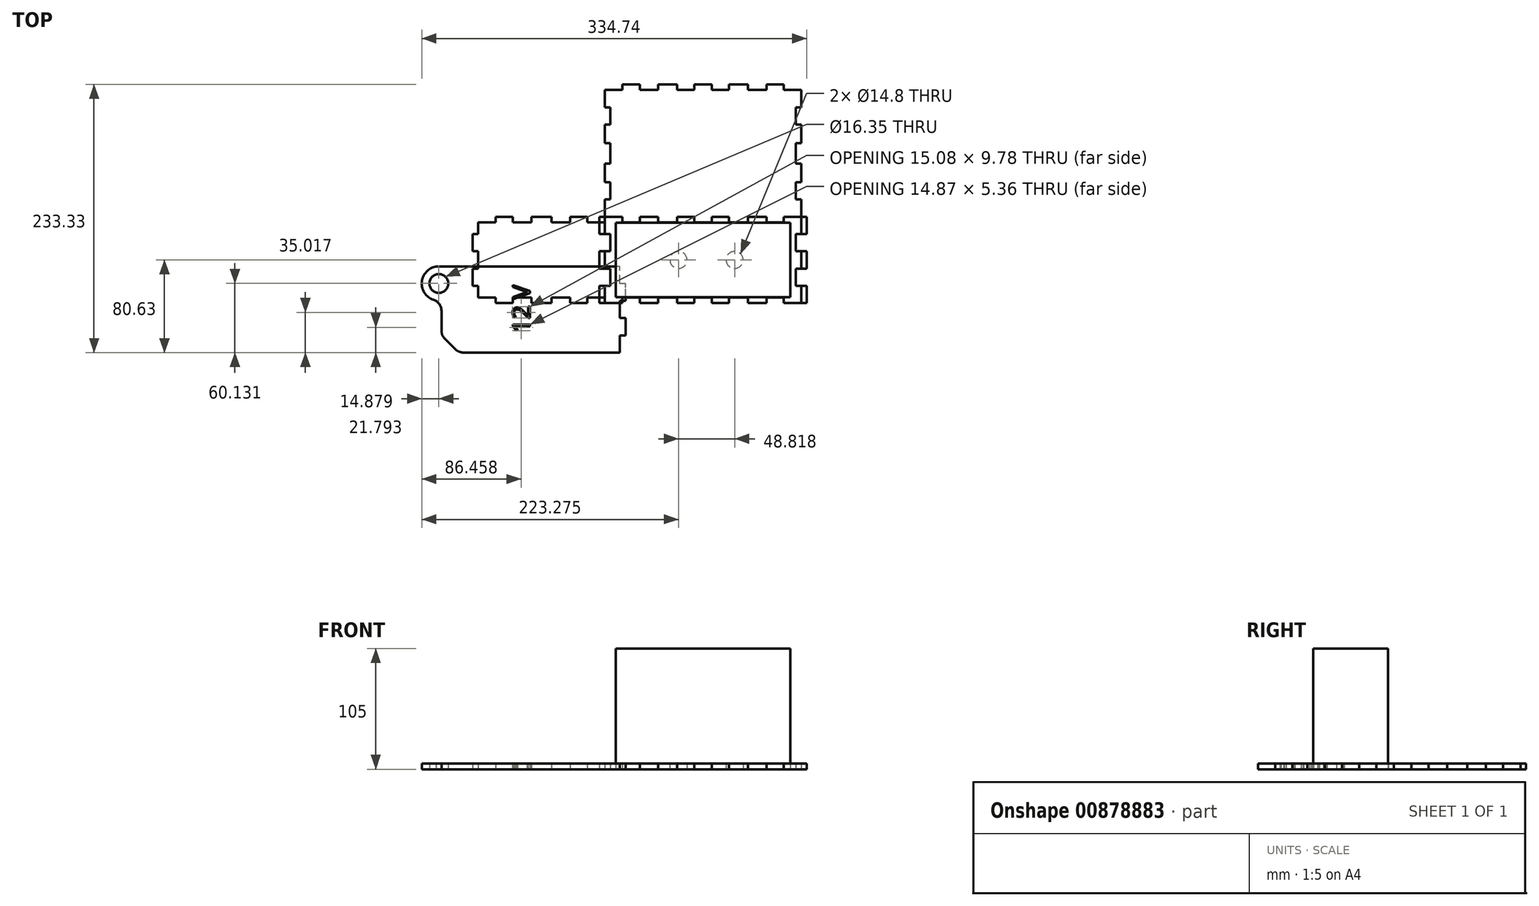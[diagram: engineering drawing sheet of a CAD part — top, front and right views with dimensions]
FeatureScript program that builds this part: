
annotation { "Feature Type Name" : "Feature", "Feature Type Description" : "" }
export const myFeature = defineFeature(function(context is Context, id is Id, definition is map)
    precondition{}
    {
        {
            assignVariable(context, id + "F0", {"name" : "MDF", "anyValue" : 4.8});
        }
        {
            var Q0;
            Q0=qCreatedBy(makeId("Top.planeOp"),FACE);
            var sketch = newSketch(context, id + "F1", { "sketchPlane" : qUnion([Q0])});
            skLineSegment(sketch, "E0", {"start": v(0, 32.5) * mm, "end": v(-76, 32.5) * mm});
            skLineSegment(sketch, "E1", {"start": v(-76, 32.5) * mm, "end": v(-76, 0) * mm});
            skLineSegment(sketch, "E2.MirrorCS", {"start": v(0, 32.5) * mm, "end": v(76, 32.5) * mm});
            skLineSegment(sketch, "E3.MirrorCS", {"start": v(76, 32.5) * mm, "end": v(76, 0) * mm});
            skLineSegment(sketch, "E4.MirrorCS", {"start": v(-76, -32.5) * mm, "end": v(-76, 0) * mm});
            skLineSegment(sketch, "E5.MirrorCS", {"start": v(0, -32.5) * mm, "end": v(-76, -32.5) * mm});
            skLineSegment(sketch, "E6.MirrorCS", {"start": v(0, -32.5) * mm, "end": v(76, -32.5) * mm});
            skLineSegment(sketch, "E7.MirrorCS", {"start": v(76, -32.5) * mm, "end": v(76, 0) * mm});
            skSolve(sketch);
        }
        {
            var Q0;
            Q0=makeQuery(id+"F1.imprint","IMPRINT",FACE,{"disambiguationData":[TD([[makeQuery(id+"F1.imprint","IMPRINT",EDGE,{"derivedFrom":sQuery(id+"F1.wireOp",EDGE,"E0")}),1.0]])]});
            extrude(context, id + "F2", {"entities" : qUnion([Q0]), "depth" : 105 * mm, "offsetDistance" : 25 * mm});
        }
        {
            var Q0;
            Q0=qCreatedBy(makeId("Top.planeOp"),FACE);
            var sketch = newSketch(context, id + "F3", { "sketchPlane" : qUnion([Q0])});
            skLineSegment(sketch, "E8", {"start": v(-85.3, 37.5) * mm, "end": v(-70.1, 37.5) * mm});
            skLineSegment(sketch, "E9", {"start": v(85.3, 37.5) * mm, "end": v(85.3, 22.5) * mm});
            skLineSegment(sketch, "E10", {"start": v(-85.3, -37.5) * mm, "end": v(-85.3, -22.5) * mm});
            skLineSegment(sketch, "E11", {"start": v(-55.1, 37.5) * mm, "end": v(-38.95, 37.5) * mm});
            skLineSegment(sketch, "E12", {"start": v(-70.1, 37.5) * mm, "end": v(-70.1, 32.7) * mm});
            skLineSegment(sketch, "E13", {"start": v(-70.1, 32.7) * mm, "end": v(-55.1, 32.7) * mm});
            skLineSegment(sketch, "E14", {"start": v(-55.1, 32.7) * mm, "end": v(-55.1, 37.5) * mm});
            skLineSegment(sketch, "E15.1.0.0", {"start": v(-38.95, 37.5) * mm, "end": v(-38.95, 32.7) * mm});
            skLineSegment(sketch, "E15.1.0.2", {"start": v(-22.5, 32.7) * mm, "end": v(-22.5, 37.5) * mm});
            skLineSegment(sketch, "E15.2.0.0", {"start": v(-7.5, 37.5) * mm, "end": v(-7.5, 32.7) * mm});
            skLineSegment(sketch, "E16.trimOffspring", {"start": v(-22.5, 37.5) * mm, "end": v(-7.5, 37.5) * mm});
            skLineSegment(sketch, "E17", {"start": v(-38.95, 32.7) * mm, "end": v(-22.5, 32.7) * mm});
            skLineSegment(sketch, "E18.MirrorCS", {"start": v(70.1, 37.5) * mm, "end": v(70.1, 32.7) * mm});
            skLineSegment(sketch, "E19.MirrorCS", {"start": v(55.1, 32.7) * mm, "end": v(55.1, 37.5) * mm});
            skLineSegment(sketch, "E20.MirrorCS", {"start": v(55.1, 37.5) * mm, "end": v(38.95, 37.5) * mm});
            skLineSegment(sketch, "E21.MirrorCS", {"start": v(38.95, 37.5) * mm, "end": v(38.95, 32.7) * mm});
            skLineSegment(sketch, "E22.MirrorCS", {"start": v(22.5, 32.7) * mm, "end": v(22.5, 37.5) * mm});
            skLineSegment(sketch, "E23.MirrorCS", {"start": v(22.5, 37.5) * mm, "end": v(7.5, 37.5) * mm});
            skLineSegment(sketch, "E24.MirrorCS", {"start": v(7.5, 37.5) * mm, "end": v(7.5, 32.7) * mm});
            skLineSegment(sketch, "E25", {"start": v(-7.5, 32.7) * mm, "end": v(7.5, 32.7) * mm});
            skLineSegment(sketch, "E26", {"start": v(22.5, 32.7) * mm, "end": v(38.95, 32.7) * mm});
            skLineSegment(sketch, "E27", {"start": v(55.1, 32.7) * mm, "end": v(70.1, 32.7) * mm});
            skLineSegment(sketch, "E28", {"start": v(-90, 92.7) * mm, "end": v(148.24, 92.7) * mm, "construction": true});
            skLineSegment(sketch, "E29", {"start": v(-85.3, 22.5) * mm, "end": v(-80.5, 22.5) * mm});
            skLineSegment(sketch, "E30", {"start": v(-80.5, 22.5) * mm, "end": v(-80.5, 7.5) * mm});
            skLineSegment(sketch, "E31", {"start": v(-80.5, 7.5) * mm, "end": v(-85.3, 7.5) * mm});
            skLineSegment(sketch, "E32.MirrorCS", {"start": v(-85.3, -22.5) * mm, "end": v(-80.5, -22.5) * mm});
            skLineSegment(sketch, "E33.MirrorCS", {"start": v(-80.5, -22.5) * mm, "end": v(-80.5, -7.5) * mm});
            skLineSegment(sketch, "E34.MirrorCS", {"start": v(-80.5, -7.5) * mm, "end": v(-85.3, -7.5) * mm});
            skLineSegment(sketch, "E35.trimOffspring", {"start": v(-85.3, -7.5) * mm, "end": v(-85.3, 7.5) * mm});
            skLineSegment(sketch, "E36.MirrorCS", {"start": v(80.5, 22.5) * mm, "end": v(80.5, 7.5) * mm});
            skLineSegment(sketch, "E37.MirrorCS", {"start": v(80.5, -22.5) * mm, "end": v(80.5, -7.5) * mm});
            skLineSegment(sketch, "E38.MirrorCS", {"start": v(80.5, 7.5) * mm, "end": v(85.3, 7.5) * mm});
            skLineSegment(sketch, "E39.MirrorCS", {"start": v(85.3, 22.5) * mm, "end": v(80.5, 22.5) * mm});
            skLineSegment(sketch, "E40.MirrorCS", {"start": v(80.5, -7.5) * mm, "end": v(85.3, -7.5) * mm});
            skLineSegment(sketch, "E41.MirrorCS", {"start": v(85.3, -22.5) * mm, "end": v(80.5, -22.5) * mm});
            skLineSegment(sketch, "E42.trimOffspring", {"start": v(85.3, 7.5) * mm, "end": v(85.3, -7.5) * mm});
            skLineSegment(sketch, "E43.trimOffspring", {"start": v(85.3, -22.5) * mm, "end": v(85.3, -37.5) * mm});
            skLineSegment(sketch, "E44.MirrorCS", {"start": v(-70.1, -32.7) * mm, "end": v(-55.1, -32.7) * mm});
            skLineSegment(sketch, "E45.MirrorCS", {"start": v(-38.95, -32.7) * mm, "end": v(-22.5, -32.7) * mm});
            skLineSegment(sketch, "E46.MirrorCS", {"start": v(-7.5, -32.7) * mm, "end": v(7.5, -32.7) * mm});
            skLineSegment(sketch, "E47.MirrorCS", {"start": v(22.5, -32.7) * mm, "end": v(38.95, -32.7) * mm});
            skLineSegment(sketch, "E48.MirrorCS", {"start": v(55.1, -32.7) * mm, "end": v(70.1, -32.7) * mm});
            skLineSegment(sketch, "E49.MirrorCS", {"start": v(-70.1, -37.5) * mm, "end": v(-70.1, -32.7) * mm});
            skLineSegment(sketch, "E50.MirrorCS", {"start": v(-55.1, -32.7) * mm, "end": v(-55.1, -37.5) * mm});
            skLineSegment(sketch, "E51.MirrorCS", {"start": v(-38.95, -37.5) * mm, "end": v(-38.95, -32.7) * mm});
            skLineSegment(sketch, "E52.MirrorCS", {"start": v(-22.5, -32.7) * mm, "end": v(-22.5, -37.5) * mm});
            skLineSegment(sketch, "E53.MirrorCS", {"start": v(-7.5, -37.5) * mm, "end": v(-7.5, -32.7) * mm});
            skLineSegment(sketch, "E54.MirrorCS", {"start": v(7.5, -37.5) * mm, "end": v(7.5, -32.7) * mm});
            skLineSegment(sketch, "E55.MirrorCS", {"start": v(22.5, -32.7) * mm, "end": v(22.5, -37.5) * mm});
            skLineSegment(sketch, "E56.MirrorCS", {"start": v(38.95, -37.5) * mm, "end": v(38.95, -32.7) * mm});
            skLineSegment(sketch, "E57.MirrorCS", {"start": v(55.1, -32.7) * mm, "end": v(55.1, -37.5) * mm});
            skLineSegment(sketch, "E58.MirrorCS", {"start": v(70.1, -37.5) * mm, "end": v(70.1, -32.7) * mm});
            skLineSegment(sketch, "E59.trimOffspring", {"start": v(-70.1, -37.5) * mm, "end": v(-85.3, -37.5) * mm});
            skLineSegment(sketch, "E60.trimOffspring", {"start": v(-38.95, -37.5) * mm, "end": v(-55.1, -37.5) * mm});
            skLineSegment(sketch, "E61.trimOffspring", {"start": v(-7.5, -37.5) * mm, "end": v(-22.5, -37.5) * mm});
            skLineSegment(sketch, "E62.trimOffspring", {"start": v(22.5, -37.5) * mm, "end": v(7.5, -37.5) * mm});
            skLineSegment(sketch, "E63.trimOffspring", {"start": v(55.1, -37.5) * mm, "end": v(38.95, -37.5) * mm});
            skLineSegment(sketch, "E64", {"start": v(70.1, 37.5) * mm, "end": v(85.3, 37.5) * mm});
            skLineSegment(sketch, "E65", {"start": v(-85.3, 22.5) * mm, "end": v(-85.3, 37.5) * mm});
            skLineSegment(sketch, "E66", {"start": v(70.1, -37.5) * mm, "end": v(85.3, -37.5) * mm});
            skLineSegment(sketch, "E67", {"start": v(-85.3, 37.5) * mm, "end": v(-164.69, 121.63) * mm, "construction": true});
            skLineSegment(sketch, "E68", {"start": v(-85.3, 37.5) * mm, "end": v(-10.38, 112.42) * mm, "construction": true});
            skLineSegment(sketch, "E69.MirrorCS", {"start": v(-85.3, 37.5) * mm, "end": v(-85.3, 52.7) * mm});
            skLineSegment(sketch, "E70.MirrorCS", {"start": v(-85.3, 67.7) * mm, "end": v(-85.3, 83.85) * mm});
            skLineSegment(sketch, "E71", {"start": v(-85.3, 52.7) * mm, "end": v(-80.5, 52.7) * mm});
            skLineSegment(sketch, "E72", {"start": v(-85.3, 67.7) * mm, "end": v(-80.5, 67.7) * mm});
            skLineSegment(sketch, "E73", {"start": v(-85.3, 83.85) * mm, "end": v(-80.5, 83.85) * mm});
            skLineSegment(sketch, "E74", {"start": v(-80.5, 67.7) * mm, "end": v(-80.5, 52.7) * mm});
            skLineSegment(sketch, "E75.MirrorCS", {"start": v(-85.3, 101.55) * mm, "end": v(-80.5, 101.55) * mm});
            skLineSegment(sketch, "E76.MirrorCS", {"start": v(-85.3, 117.7) * mm, "end": v(-80.5, 117.7) * mm});
            skLineSegment(sketch, "E77.MirrorCS", {"start": v(-85.3, 132.7) * mm, "end": v(-80.5, 132.7) * mm});
            skLineSegment(sketch, "E78", {"start": v(-80.5, 83.85) * mm, "end": v(-80.5, 101.55) * mm});
            skLineSegment(sketch, "E79", {"start": v(-85.3, 101.55) * mm, "end": v(-85.3, 117.7) * mm});
            skLineSegment(sketch, "E80", {"start": v(-80.5, 117.7) * mm, "end": v(-80.5, 132.7) * mm});
            skLineSegment(sketch, "E81", {"start": v(-85.3, 132.7) * mm, "end": v(-85.3, 147.9) * mm});
            skLineSegment(sketch, "E82.MirrorCS", {"start": v(-85.3, 147.9) * mm, "end": v(-70.1, 147.9) * mm});
            skLineSegment(sketch, "E83.MirrorCS", {"start": v(-70.1, 147.9) * mm, "end": v(-70.1, 152.7) * mm});
            skLineSegment(sketch, "E84.MirrorCS", {"start": v(-70.1, 152.7) * mm, "end": v(-55.1, 152.7) * mm});
            skLineSegment(sketch, "E85.MirrorCS", {"start": v(-55.1, 152.7) * mm, "end": v(-55.1, 147.9) * mm});
            skLineSegment(sketch, "E86.MirrorCS", {"start": v(-55.1, 147.9) * mm, "end": v(-38.95, 147.9) * mm});
            skLineSegment(sketch, "E87.MirrorCS", {"start": v(-38.95, 147.9) * mm, "end": v(-38.95, 152.7) * mm});
            skLineSegment(sketch, "E88.MirrorCS", {"start": v(-38.95, 152.7) * mm, "end": v(-22.5, 152.7) * mm});
            skLineSegment(sketch, "E89.MirrorCS", {"start": v(-22.5, 152.7) * mm, "end": v(-22.5, 147.9) * mm});
            skLineSegment(sketch, "E90.MirrorCS", {"start": v(-22.5, 147.9) * mm, "end": v(-7.5, 147.9) * mm});
            skLineSegment(sketch, "E91.MirrorCS", {"start": v(-7.5, 147.9) * mm, "end": v(-7.5, 152.7) * mm});
            skLineSegment(sketch, "E92.MirrorCS", {"start": v(-7.5, 152.7) * mm, "end": v(7.5, 152.7) * mm});
            skLineSegment(sketch, "E93.MirrorCS", {"start": v(7.5, 147.9) * mm, "end": v(7.5, 152.7) * mm});
            skLineSegment(sketch, "E94.MirrorCS", {"start": v(22.5, 147.9) * mm, "end": v(7.5, 147.9) * mm});
            skLineSegment(sketch, "E95.MirrorCS", {"start": v(22.5, 152.7) * mm, "end": v(22.5, 147.9) * mm});
            skLineSegment(sketch, "E96.MirrorCS", {"start": v(22.5, 152.7) * mm, "end": v(38.95, 152.7) * mm});
            skLineSegment(sketch, "E97.MirrorCS", {"start": v(38.95, 147.9) * mm, "end": v(38.95, 152.7) * mm});
            skLineSegment(sketch, "E98.MirrorCS", {"start": v(55.1, 147.9) * mm, "end": v(38.95, 147.9) * mm});
            skLineSegment(sketch, "E99.MirrorCS", {"start": v(55.1, 152.7) * mm, "end": v(55.1, 147.9) * mm});
            skLineSegment(sketch, "E100.MirrorCS", {"start": v(55.1, 152.7) * mm, "end": v(70.1, 152.7) * mm});
            skLineSegment(sketch, "E101.MirrorCS", {"start": v(70.1, 147.9) * mm, "end": v(70.1, 152.7) * mm});
            skLineSegment(sketch, "E102.MirrorCS", {"start": v(70.1, 147.9) * mm, "end": v(85.3, 147.9) * mm});
            skLineSegment(sketch, "E103.MirrorCS", {"start": v(85.3, 132.7) * mm, "end": v(85.3, 147.9) * mm});
            skLineSegment(sketch, "E104.MirrorCS", {"start": v(85.3, 132.7) * mm, "end": v(80.5, 132.7) * mm});
            skLineSegment(sketch, "E105.MirrorCS", {"start": v(80.5, 117.7) * mm, "end": v(80.5, 132.7) * mm});
            skLineSegment(sketch, "E106.MirrorCS", {"start": v(85.3, 117.7) * mm, "end": v(80.5, 117.7) * mm});
            skLineSegment(sketch, "E107.MirrorCS", {"start": v(85.3, 101.55) * mm, "end": v(85.3, 117.7) * mm});
            skLineSegment(sketch, "E108.MirrorCS", {"start": v(85.3, 101.55) * mm, "end": v(80.5, 101.55) * mm});
            skLineSegment(sketch, "E109.MirrorCS", {"start": v(80.5, 83.85) * mm, "end": v(80.5, 101.55) * mm});
            skLineSegment(sketch, "E110.MirrorCS", {"start": v(85.3, 83.85) * mm, "end": v(80.5, 83.85) * mm});
            skLineSegment(sketch, "E111.MirrorCS", {"start": v(85.3, 67.7) * mm, "end": v(80.5, 67.7) * mm});
            skLineSegment(sketch, "E112.MirrorCS", {"start": v(80.5, 67.7) * mm, "end": v(80.5, 52.7) * mm});
            skLineSegment(sketch, "E113.MirrorCS", {"start": v(85.3, 52.7) * mm, "end": v(80.5, 52.7) * mm});
            skLineSegment(sketch, "E114", {"start": v(85.3, 83.85) * mm, "end": v(85.3, 67.7) * mm});
            skLineSegment(sketch, "E115", {"start": v(85.3, 52.7) * mm, "end": v(85.3, 37.5) * mm});
            skLineSegment(sketch, "E116", {"start": v(-85.3, 32.68) * mm, "end": v(-100.5, 32.68) * mm});
            skLineSegment(sketch, "E117", {"start": v(-140.5, 30.09) * mm, "end": v(-140.5, -11.59) * mm, "construction": true});
            skLineSegment(sketch, "E118.MirrorCS", {"start": v(-195.7, 22.5) * mm, "end": v(-200.5, 22.5) * mm});
            skLineSegment(sketch, "E119.MirrorCS", {"start": v(-200.5, 22.5) * mm, "end": v(-200.5, 7.5) * mm});
            skLineSegment(sketch, "E120.MirrorCS", {"start": v(-200.5, 7.5) * mm, "end": v(-195.7, 7.5) * mm});
            skLineSegment(sketch, "E121.MirrorCS", {"start": v(-195.7, -7.5) * mm, "end": v(-195.7, 7.5) * mm});
            skLineSegment(sketch, "E122.MirrorCS", {"start": v(-200.5, -22.5) * mm, "end": v(-200.5, -7.5) * mm});
            skLineSegment(sketch, "E123.MirrorCS", {"start": v(-195.7, -22.5) * mm, "end": v(-200.5, -22.5) * mm});
            skLineSegment(sketch, "E124.MirrorCS", {"start": v(-200.5, -7.5) * mm, "end": v(-195.7, -7.5) * mm});
            skLineSegment(sketch, "E125", {"start": v(-100.5, 32.68) * mm, "end": v(-100.5, 37.48) * mm});
            skLineSegment(sketch, "E126", {"start": v(-100.5, 37.48) * mm, "end": v(-115.5, 37.48) * mm});
            skLineSegment(sketch, "E127", {"start": v(-115.5, 37.48) * mm, "end": v(-115.5, 32.68) * mm});
            skLineSegment(sketch, "E128", {"start": v(-115.5, 32.68) * mm, "end": v(-131.65, 32.68) * mm});
            skLineSegment(sketch, "E129", {"start": v(-131.65, 32.68) * mm, "end": v(-131.65, 37.48) * mm});
            skLineSegment(sketch, "E130", {"start": v(-131.65, 37.48) * mm, "end": v(-149.35, 37.48) * mm});
            skLineSegment(sketch, "E131", {"start": v(-149.35, 37.48) * mm, "end": v(-149.35, 32.68) * mm});
            skLineSegment(sketch, "E132", {"start": v(-149.35, 32.68) * mm, "end": v(-165.5, 32.68) * mm});
            skLineSegment(sketch, "E133", {"start": v(-165.5, 32.68) * mm, "end": v(-165.5, 37.48) * mm});
            skLineSegment(sketch, "E134", {"start": v(-165.5, 37.48) * mm, "end": v(-180.5, 37.48) * mm});
            skLineSegment(sketch, "E135", {"start": v(-180.5, 37.48) * mm, "end": v(-180.5, 32.68) * mm});
            skLineSegment(sketch, "E136", {"start": v(-195.7, 22.5) * mm, "end": v(-195.7, 32.68) * mm});
            skLineSegment(sketch, "E137", {"start": v(-195.7, 32.68) * mm, "end": v(-180.5, 32.68) * mm});
            skLineSegment(sketch, "E138.MirrorCS", {"start": v(-195.7, -22.5) * mm, "end": v(-195.7, -32.68) * mm});
            skLineSegment(sketch, "E139.MirrorCS", {"start": v(-195.7, -32.68) * mm, "end": v(-180.5, -32.68) * mm});
            skLineSegment(sketch, "E140.MirrorCS", {"start": v(-180.5, -37.48) * mm, "end": v(-180.5, -32.68) * mm});
            skLineSegment(sketch, "E141.MirrorCS", {"start": v(-165.5, -37.48) * mm, "end": v(-180.5, -37.48) * mm});
            skLineSegment(sketch, "E142.MirrorCS", {"start": v(-165.5, -32.68) * mm, "end": v(-165.5, -37.48) * mm});
            skLineSegment(sketch, "E143.MirrorCS", {"start": v(-149.35, -32.68) * mm, "end": v(-165.5, -32.68) * mm});
            skLineSegment(sketch, "E144.MirrorCS", {"start": v(-149.35, -37.48) * mm, "end": v(-149.35, -32.68) * mm});
            skLineSegment(sketch, "E145.MirrorCS", {"start": v(-131.65, -37.48) * mm, "end": v(-149.35, -37.48) * mm});
            skLineSegment(sketch, "E146.MirrorCS", {"start": v(-131.65, -32.68) * mm, "end": v(-131.65, -37.48) * mm});
            skLineSegment(sketch, "E147.MirrorCS", {"start": v(-115.5, -32.68) * mm, "end": v(-131.65, -32.68) * mm});
            skLineSegment(sketch, "E148.MirrorCS", {"start": v(-115.5, -37.48) * mm, "end": v(-115.5, -32.68) * mm});
            skLineSegment(sketch, "E149.MirrorCS", {"start": v(-100.5, -37.48) * mm, "end": v(-115.5, -37.48) * mm});
            skLineSegment(sketch, "E150.MirrorCS", {"start": v(-100.5, -32.68) * mm, "end": v(-100.5, -37.48) * mm});
            skLineSegment(sketch, "E151.MirrorCS", {"start": v(-85.3, -32.68) * mm, "end": v(-100.5, -32.68) * mm});
            skPoint(sketch, "E152.orphan", {"position": v(-85.3, 147.7) * mm});
            skPoint(sketch, "E153.orphan", {"position": v(85.3, 147.7) * mm});
            skLineSegment(sketch, "E154", {"start": v(-90.1, -47.42) * mm, "end": v(-90.1, 52.34) * mm, "construction": true});
            skLineSegment(sketch, "E155", {"start": v(-85.3, -37.5) * mm, "end": v(-90.1, -37.5) * mm});
            skLineSegment(sketch, "E156", {"start": v(-90.1, -37.5) * mm, "end": v(-90.1, -22.5) * mm});
            skLineSegment(sketch, "E157", {"start": v(-90.1, -22.5) * mm, "end": v(-85.3, -22.5) * mm});
            skLineSegment(sketch, "E158", {"start": v(-85.3, -7.5) * mm, "end": v(-90.1, -7.5) * mm});
            skLineSegment(sketch, "E159", {"start": v(-90.1, -7.5) * mm, "end": v(-90.1, 7.5) * mm});
            skLineSegment(sketch, "E160", {"start": v(-90.1, 7.5) * mm, "end": v(-85.3, 7.5) * mm});
            skLineSegment(sketch, "E161", {"start": v(-85.3, 22.5) * mm, "end": v(-90.1, 22.5) * mm});
            skLineSegment(sketch, "E162", {"start": v(-90.1, 22.5) * mm, "end": v(-90.1, 37.5) * mm});
            skLineSegment(sketch, "E163", {"start": v(-90.1, 37.5) * mm, "end": v(-85.3, 37.5) * mm});
            skLineSegment(sketch, "E164", {"start": v(90.1, 42.57) * mm, "end": v(90.1, -53.63) * mm, "construction": true});
            skLineSegment(sketch, "E165", {"start": v(85.3, 37.5) * mm, "end": v(90.1, 37.5) * mm});
            skLineSegment(sketch, "E166", {"start": v(90.1, 37.5) * mm, "end": v(90.1, 22.5) * mm});
            skLineSegment(sketch, "E167", {"start": v(90.1, 22.5) * mm, "end": v(85.3, 22.5) * mm});
            skLineSegment(sketch, "E168", {"start": v(85.3, 7.5) * mm, "end": v(90.1, 7.5) * mm});
            skLineSegment(sketch, "E169", {"start": v(90.1, 7.5) * mm, "end": v(90.1, -7.5) * mm});
            skLineSegment(sketch, "E170", {"start": v(90.1, -7.5) * mm, "end": v(85.3, -7.5) * mm});
            skLineSegment(sketch, "E171", {"start": v(85.3, -22.5) * mm, "end": v(90.1, -22.5) * mm});
            skLineSegment(sketch, "E172", {"start": v(90.1, -22.5) * mm, "end": v(90.1, -37.54) * mm});
            skLineSegment(sketch, "E173", {"start": v(90.1, -37.54) * mm, "end": v(83.17, -37.5) * mm});
            skLineSegment(sketch, "E174", {"start": v(65.44, -32.7) * mm, "end": v(-231.34, -32.7) * mm, "construction": true});
            skLineSegment(sketch, "E175", {"start": v(66.76, 32.7) * mm, "end": v(-200.15, 32.7) * mm, "construction": true});
            skCircle(sketch, "E176", {"center": v(27.45, 0) * mm, "radius": 7.4 * mm});
            skCircle(sketch, "E177", {"center": v(-21.36, 0) * mm, "radius": 7.4 * mm});
            skSolve(sketch);
        }
        {
            var Q0;
            Q0=qCreatedBy(makeId("Top.planeOp"),FACE);
            var sketch = newSketch(context, id + "F4", { "sketchPlane" : qUnion([Q0])});
            skLineSegment(sketch, "E178", {"start": v(-208.33, -80.63) * mm, "end": v(-72.27, -80.63) * mm});
            skLineSegment(sketch, "E179", {"start": v(-67.47, -65.63) * mm, "end": v(-67.47, -50.63) * mm});
            skLineSegment(sketch, "E180", {"start": v(-67.47, -20.63) * mm, "end": v(-72.27, -20.63) * mm});
            skLineSegment(sketch, "E181", {"start": v(-67.47, -35.63) * mm, "end": v(-72.27, -35.63) * mm});
            skLineSegment(sketch, "E182", {"start": v(-67.47, -50.63) * mm, "end": v(-72.27, -50.63) * mm});
            skLineSegment(sketch, "E183", {"start": v(-67.47, -65.63) * mm, "end": v(-72.27, -65.63) * mm});
            skLineSegment(sketch, "E184", {"start": v(-72.27, -20.63) * mm, "end": v(-72.27, -5.63) * mm});
            skLineSegment(sketch, "E185", {"start": v(-72.27, -35.63) * mm, "end": v(-72.27, -50.63) * mm});
            skLineSegment(sketch, "E186.trimOffspring", {"start": v(-67.47, -35.63) * mm, "end": v(-67.47, -20.63) * mm});
            skLineSegment(sketch, "E187", {"start": v(-72.27, -65.63) * mm, "end": v(-72.27, -80.63) * mm});
            skLineSegment(sketch, "E188", {"start": v(-197.47, -86.62) * mm, "end": v(-197.47, 29.14) * mm, "construction": true});
            skLineSegment(sketch, "E189", {"start": v(-224.54, -68.56) * mm, "end": v(-215.4, -77.7) * mm});
            skArc(sketch, "E190.filletArc", {"start": v(-227.47, -61.49) * mm, "mid": v(-226.7, -65.31) * mm, "end": v(-224.54, -68.56) * mm});
            skArc(sketch, "E191.filletArc", {"start": v(-215.4, -77.7) * mm, "mid": v(-212.15, -79.87) * mm, "end": v(-208.33, -80.63) * mm});
            skText(sketch, "E192", { "text": "12 V", "fontName": "OpenSans-Regular.ttf"});
            skPoint(sketch, "E193.filletArc.center.orphan", {"position": v(-208.33, -15.63) * mm});
            skCircle(sketch, "E194", {"center": v(-229.76, -20.5) * mm, "radius": 8.18 * mm});
            skArc(sketch, "E195", {"start": v(-232.05, -5.8) * mm, "mid": v(-244.6, -19.3) * mm, "end": v(-234.37, -34.65) * mm});
            skLineSegment(sketch, "E196.trimOffspring", {"start": v(-227.47, -44.16) * mm, "end": v(-227.47, -61.49) * mm});
            skLineSegment(sketch, "E197", {"start": v(-72.27, -5.63) * mm, "end": v(-232.05, -5.8) * mm});
            skPoint(sketch, "E198.visualSharp", {"position": v(-227.47, -35.2) * mm});
            skArc(sketch, "E198.filletArc", {"start": v(-227.47, -44.16) * mm, "mid": v(-229.38, -38.28) * mm, "end": v(-234.37, -34.65) * mm});
            const initialGuessF4  = {"E192": [-0.15064, -0.06343, 0, 1, 0.015]};
            skSetInitialGuess(sketch, initialGuessF4);
            skSolve(sketch);
        }
        {
            var Q0;
            {var subQ3=sQuery(id+"F3.wireOp",EDGE,"E8");Q0=makeQuery(id+"F3.imprint","IMPRINT",FACE,{"disambiguationData":[TD([[makeQuery(id+"F3.imprint","IMPRINT",EDGE,{"derivedFrom":subQ3}),-1.0]])]});}
            extrude(context, id + "F5", {"entities" : qUnion([Q0]), "depth" : (getVariable(context, 'MDF')) * mm, "offsetDistance" : 25 * mm});
        }
        {
            var Q0;
            Q0=makeQuery(id+"F4.imprint","IMPRINT",FACE,{"disambiguationData":[TD([[makeQuery(id+"F4.imprint","IMPRINT",EDGE,{"derivedFrom":sQuery(id+"F4.wireOp",EDGE,"E178")}),1.0]])]});
            extrude(context, id + "F6", {"entities" : qUnion([Q0]), "depth" : (getVariable(context, 'MDF')) * mm, "offsetDistance" : 25 * mm});
        }
        {
            var Q0;
            {var subQ0=sQuery(id+"F3.wireOp",EDGE,"E29");Q0=makeQuery(id+"F3.imprint","IMPRINT",FACE,{"disambiguationData":[TD([[makeQuery(id+"F3.imprint","IMPRINT",EDGE,{"derivedFrom":subQ0}),-1.0]])]});}
            var Q1;
            {var subQ0=sQuery(id+"F3.wireOp",EDGE,"E161");Q1=makeQuery(id+"F3.imprint","IMPRINT",FACE,{"disambiguationData":[TD([[makeQuery(id+"F3.imprint","IMPRINT",EDGE,{"derivedFrom":subQ0}),-1.0]])]});}
            var Q2;
            Q2=makeQuery(id+"F3.imprint","IMPRINT",FACE,{"disambiguationData":[TD([[makeQuery(id+"F3.imprint","IMPRINT",EDGE,{"derivedFrom":sQuery(id+"F3.wireOp",EDGE,"E35.trimOffspring")}),1.0]])]});
            var Q3;
            {var subQ0=sQuery(id+"F3.wireOp",EDGE,"E157");Q3=makeQuery(id+"F3.imprint","IMPRINT",FACE,{"disambiguationData":[TD([[makeQuery(id+"F3.imprint","IMPRINT",EDGE,{"derivedFrom":subQ0}),-1.0]])]});}
            extrude(context, id + "F7", {"entities" : qUnion([Q0, Q1, Q2, Q3]), "depth" : (getVariable(context, 'MDF')) * mm, "offsetDistance" : 25 * mm});
        }
        {
            var Q0;
            Q0=makeQuery(id+"F3.imprint","IMPRINT",FACE,{"disambiguationData":[TD([[makeQuery(id+"F3.imprint","IMPRINT",EDGE,{"derivedFrom":sQuery(id+"F3.wireOp",EDGE,"E8")}),1.0]])]});
            extrude(context, id + "F8", {"entities" : qUnion([Q0]), "depth" : (getVariable(context, 'MDF')) * mm, "offsetDistance" : 25 * mm});
        }
        {
            var Q0;
            {var subQ2=sQuery(id+"F3.wireOp",EDGE,"E8");Q0=makeQuery(id+"F3.imprint","IMPRINT",FACE,{"disambiguationData":[TD([[makeQuery(id+"F3.imprint","IMPRINT",EDGE,{"derivedFrom":subQ2}),-1.0]])]});}
            var Q1;
            {var subQ0=sQuery(id+"F3.wireOp",EDGE,"E161");Q1=makeQuery(id+"F3.imprint","IMPRINT",FACE,{"disambiguationData":[TD([[makeQuery(id+"F3.imprint","IMPRINT",EDGE,{"derivedFrom":subQ0}),-1.0]])]});}
            var Q2;
            {var subQ0=sQuery(id+"F3.wireOp",EDGE,"E163");Q2=makeQuery(id+"F3.imprint","IMPRINT",FACE,{"disambiguationData":[TD([[makeQuery(id+"F3.imprint","IMPRINT",EDGE,{"derivedFrom":subQ0}),-1.0]])]});}
            var Q3;
            Q3=makeQuery(id+"F3.imprint","IMPRINT",FACE,{"disambiguationData":[TD([[makeQuery(id+"F3.imprint","IMPRINT",EDGE,{"derivedFrom":sQuery(id+"F3.wireOp",EDGE,"E35.trimOffspring")}),1.0]])]});
            var Q4;
            {var subQ0=sQuery(id+"F3.wireOp",EDGE,"E157");Q4=makeQuery(id+"F3.imprint","IMPRINT",FACE,{"disambiguationData":[TD([[makeQuery(id+"F3.imprint","IMPRINT",EDGE,{"derivedFrom":subQ0}),-1.0]])]});}
            var Q5;
            {var subQ0=sQuery(id+"F3.wireOp",EDGE,"E155");Q5=makeQuery(id+"F3.imprint","IMPRINT",FACE,{"disambiguationData":[TD([[makeQuery(id+"F3.imprint","IMPRINT",EDGE,{"derivedFrom":subQ0}),-1.0]])]});}
            var Q6;
            Q6=makeQuery(id+"F3.imprint","IMPRINT",FACE,{"disambiguationData":[TD([[makeQuery(id+"F3.imprint","IMPRINT",EDGE,{"derivedFrom":sQuery(id+"F3.wireOp",EDGE,"E9")}),1.0]])]});
            var Q7;
            Q7=makeQuery(id+"F3.imprint","IMPRINT",FACE,{"disambiguationData":[TD([[makeQuery(id+"F3.imprint","IMPRINT",EDGE,{"derivedFrom":sQuery(id+"F3.wireOp",EDGE,"E42.trimOffspring")}),1.0]])]});
            var Q8;
            {var subQ1=sQuery(id+"F3.wireOp",EDGE,"E43.trimOffspring");Q8=makeQuery(id+"F3.imprint","IMPRINT",FACE,{"disambiguationData":[TD([[makeQuery(id+"F3.imprint","IMPRINT",EDGE,{"derivedFrom":subQ1}),1.0]])]});}
            var Q9;
            Q9=makeQuery(id+"F3.imprint","IMPRINT",FACE,{"disambiguationData":[TD([[makeQuery(id+"F3.imprint","IMPRINT",EDGE,{"derivedFrom":sQuery(id+"F3.wireOp",EDGE,"E177")}),1.0]])]});
            var Q10;
            Q10=makeQuery(id+"F3.imprint","IMPRINT",FACE,{"disambiguationData":[TD([[makeQuery(id+"F3.imprint","IMPRINT",EDGE,{"derivedFrom":sQuery(id+"F3.wireOp",EDGE,"E176")}),1.0]])]});
            extrude(context, id + "F9", {"entities" : qUnion([Q0, Q1, Q2, Q3, Q4, Q5, Q6, Q7, Q8, Q9, Q10]), "depth" : (getVariable(context, 'MDF')) * mm, "offsetDistance" : 25 * mm});
        }
    });
